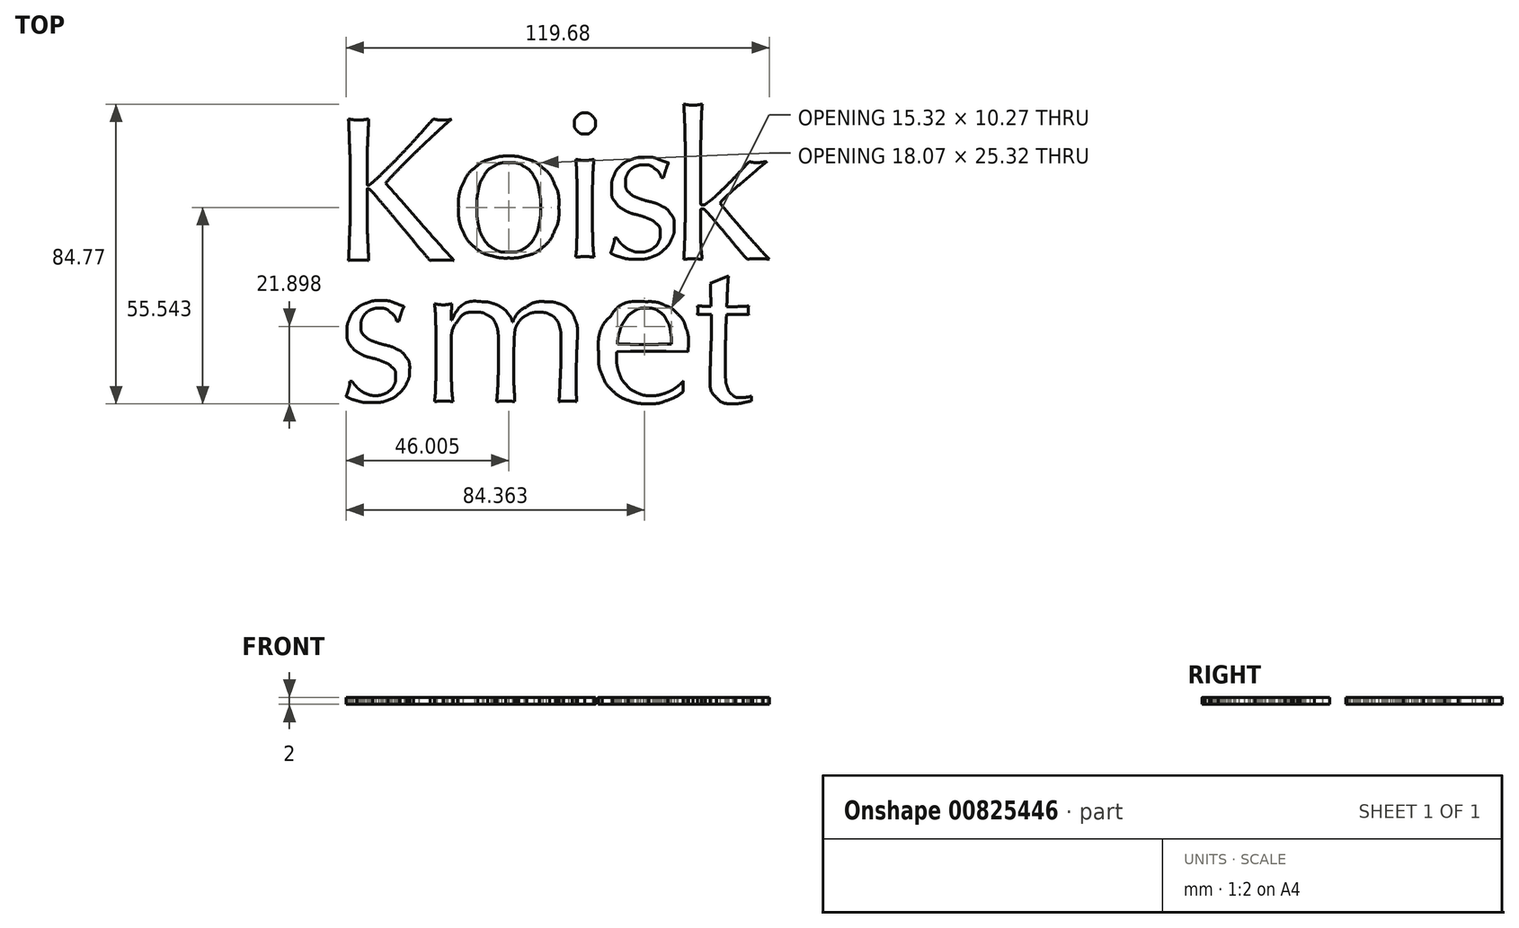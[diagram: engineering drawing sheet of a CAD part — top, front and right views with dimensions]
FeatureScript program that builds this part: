
annotation { "Feature Type Name" : "Feature", "Feature Type Description" : "" }
export const myFeature = defineFeature(function(context is Context, id is Id, definition is map)
    precondition{}
    {
        {
            var Q0;
            Q0=qCreatedBy(makeId("Top.planeOp"),FACE);
            var sketch = newSketch(context, id + "F0", { "sketchPlane" : qUnion([Q0])});
            skFitSpline(sketch, "E0", {"points": [v(-58.08, -1.08) * mm, v(-57.19, -1) * mm, v(-56.23, -0.96) * mm, v(-55.23, -0.96) * mm]});
            skFitSpline(sketch, "E1", {"points": [v(-55.23, -0.96) * mm, v(-54.22, -0.96) * mm, v(-53.27, -1) * mm, v(-52.37, -1.08) * mm]});
            skFitSpline(sketch, "E2", {"points": [v(-52.37, -1.08) * mm, v(-52.49, 1.33) * mm, v(-52.6, 3.78) * mm, v(-52.72, 6.26) * mm]});
            skFitSpline(sketch, "E3", {"points": [v(-52.72, 6.26) * mm, v(-52.8, 8.75) * mm, v(-52.84, 11.27) * mm, v(-52.84, 13.83) * mm]});
            skFitSpline(sketch, "E4", {"points": [v(-52.84, 18.9) * mm, v(-52.84, 19.13) * mm, v(-52.74, 19.25) * mm, v(-52.55, 19.25) * mm]});
            skFitSpline(sketch, "E5", {"points": [v(-52.55, 19.25) * mm, v(-52.4, 19.25) * mm, v(-52.16, 19.09) * mm, v(-51.85, 18.78) * mm]});
            skFitSpline(sketch, "E6", {"points": [v(-51.85, 18.78) * mm, v(-51.23, 18.16) * mm, v(-50.28, 17.07) * mm, v(-49, 15.52) * mm]});
            skFitSpline(sketch, "E7", {"points": [v(-49, 15.52) * mm, v(-47.68, 14) * mm, v(-46.22, 12.28) * mm, v(-44.63, 10.34) * mm]});
            skFitSpline(sketch, "E8", {"points": [v(-44.63, 10.34) * mm, v(-43, 8.43) * mm, v(-41.35, 6.46) * mm, v(-39.68, 4.4) * mm]});
            skFitSpline(sketch, "E9", {"points": [v(-39.68, 4.4) * mm, v(-37.97, 2.34) * mm, v(-36.42, 0.52) * mm, v(-35.02, -1.08) * mm]});
            skFitSpline(sketch, "E10", {"points": [v(-35.02, -1.08) * mm, v(-34.48, -1) * mm, v(-33.95, -0.96) * mm, v(-33.45, -0.96) * mm]});
            skFitSpline(sketch, "E11", {"points": [v(-33.45, -0.96) * mm, v(-32.9, -0.96) * mm, v(-32.36, -0.96) * mm, v(-31.82, -0.96) * mm]});
            skFitSpline(sketch, "E12", {"points": [v(-31.82, -0.96) * mm, v(-31.24, -0.96) * mm, v(-30.65, -0.96) * mm, v(-30.07, -0.96) * mm]});
            skFitSpline(sketch, "E13", {"points": [v(-30.07, -0.96) * mm, v(-29.5, -0.96) * mm, v(-28.9, -1) * mm, v(-28.33, -1.08) * mm]});
            skFitSpline(sketch, "E14", {"points": [v(-28.33, -1.08) * mm, v(-31.63, 2.61) * mm, v(-34.89, 6.28) * mm, v(-38.1, 9.93) * mm]});
            skFitSpline(sketch, "E15", {"points": [v(-38.1, 9.93) * mm, v(-41.3, 13.62) * mm, v(-44.45, 17.23) * mm, v(-47.6, 20.76) * mm]});
            skFitSpline(sketch, "E16", {"points": [v(-47.6, 20.76) * mm, v(-46.55, 21.96) * mm, v(-45.25, 23.36) * mm, v(-43.7, 24.95) * mm]});
            skFitSpline(sketch, "E17", {"points": [v(-43.7, 24.95) * mm, v(-42.1, 26.58) * mm, v(-40.46, 28.23) * mm, v(-38.75, 29.9) * mm]});
            skFitSpline(sketch, "E18", {"points": [v(-38.75, 29.9) * mm, v(-37, 31.57) * mm, v(-35.27, 33.2) * mm, v(-33.57, 34.8) * mm]});
            skFitSpline(sketch, "E19", {"points": [v(-33.57, 34.8) * mm, v(-31.86, 36.38) * mm, v(-30.32, 37.76) * mm, v(-28.97, 38.92) * mm]});
            skFitSpline(sketch, "E20", {"points": [v(-28.97, 38.92) * mm, v(-29.43, 38.85) * mm, v(-29.9, 38.77) * mm, v(-30.36, 38.7) * mm]});
            skFitSpline(sketch, "E21", {"points": [v(-30.36, 38.7) * mm, v(-30.83, 38.65) * mm, v(-31.3, 38.63) * mm, v(-31.76, 38.63) * mm]});
            skFitSpline(sketch, "E22", {"points": [v(-31.76, 38.63) * mm, v(-32.15, 38.63) * mm, v(-32.54, 38.65) * mm, v(-32.93, 38.7) * mm]});
            skFitSpline(sketch, "E23", {"points": [v(-32.93, 38.7) * mm, v(-33.31, 38.77) * mm, v(-33.72, 38.85) * mm, v(-34.15, 38.92) * mm]});
            skFitSpline(sketch, "E24", {"points": [v(-34.15, 38.92) * mm, v(-35.5, 37.37) * mm, v(-36.92, 35.76) * mm, v(-38.4, 34.1) * mm]});
            skFitSpline(sketch, "E25", {"points": [v(-38.4, 34.1) * mm, v(-39.87, 32.46) * mm, v(-41.37, 30.85) * mm, v(-42.88, 29.26) * mm]});
            skFitSpline(sketch, "E26", {"points": [v(-42.88, 29.26) * mm, v(-44.4, 27.67) * mm, v(-45.9, 26.13) * mm, v(-47.42, 24.66) * mm]});
            skFitSpline(sketch, "E27", {"points": [v(-47.42, 24.66) * mm, v(-48.9, 23.18) * mm, v(-50.32, 21.87) * mm, v(-51.67, 20.7) * mm]});
            skFitSpline(sketch, "E28", {"points": [v(-51.67, 20.7) * mm, v(-52.06, 20.35) * mm, v(-52.33, 20.18) * mm, v(-52.49, 20.18) * mm]});
            skFitSpline(sketch, "E29", {"points": [v(-52.49, 20.18) * mm, v(-52.72, 20.18) * mm, v(-52.84, 20.33) * mm, v(-52.84, 20.64) * mm]});
            skLineSegment(sketch, "E30", {"start": v(-52.84, 13.83) * mm, "end": v(-52.84, 18.9) * mm});
            skLineSegment(sketch, "E31", {"start": v(-52.84, 18.9) * mm, "end": v(-52.84, 13.83) * mm});
            skFitSpline(sketch, "E32", {"points": [v(-52.84, 23.84) * mm, v(-52.84, 26.4) * mm, v(-52.8, 28.91) * mm, v(-52.72, 31.36) * mm]});
            skFitSpline(sketch, "E33", {"points": [v(-52.72, 31.36) * mm, v(-52.6, 33.84) * mm, v(-52.49, 36.36) * mm, v(-52.37, 38.92) * mm]});
            skFitSpline(sketch, "E34", {"points": [v(-52.37, 38.92) * mm, v(-52.88, 38.85) * mm, v(-53.36, 38.77) * mm, v(-53.83, 38.7) * mm]});
            skFitSpline(sketch, "E35", {"points": [v(-53.83, 38.7) * mm, v(-54.3, 38.65) * mm, v(-54.76, 38.63) * mm, v(-55.23, 38.63) * mm]});
            skFitSpline(sketch, "E36", {"points": [v(-55.23, 38.63) * mm, v(-55.7, 38.63) * mm, v(-56.16, 38.65) * mm, v(-56.62, 38.7) * mm]});
            skFitSpline(sketch, "E37", {"points": [v(-56.62, 38.7) * mm, v(-57.09, 38.77) * mm, v(-57.57, 38.85) * mm, v(-58.08, 38.92) * mm]});
            skFitSpline(sketch, "E38", {"points": [v(-58.08, 38.92) * mm, v(-57.96, 36.36) * mm, v(-57.86, 33.84) * mm, v(-57.79, 31.36) * mm]});
            skFitSpline(sketch, "E39", {"points": [v(-57.79, 31.36) * mm, v(-57.67, 28.91) * mm, v(-57.61, 26.4) * mm, v(-57.61, 23.84) * mm]});
            skLineSegment(sketch, "E40", {"start": v(-52.84, 20.64) * mm, "end": v(-52.84, 23.84) * mm});
            skLineSegment(sketch, "E41", {"start": v(-52.84, 23.84) * mm, "end": v(-52.84, 20.64) * mm});
            skFitSpline(sketch, "E42", {"points": [v(-57.61, 13.83) * mm, v(-57.61, 11.27) * mm, v(-57.67, 8.75) * mm, v(-57.79, 6.26) * mm]});
            skFitSpline(sketch, "E43", {"points": [v(-57.79, 6.26) * mm, v(-57.86, 3.78) * mm, v(-57.96, 1.33) * mm, v(-58.08, -1.08) * mm]});
            skLineSegment(sketch, "E44", {"start": v(-57.61, 23.84) * mm, "end": v(-57.61, 13.83) * mm});
            skLineSegment(sketch, "E45", {"start": v(-57.61, 13.83) * mm, "end": v(-57.61, 23.84) * mm});
            skFitSpline(sketch, "E46", {"points": [v(-21.81, 13.91) * mm, v(-21.81, 15.54) * mm, v(-21.67, 17.12) * mm, v(-21.4, 18.63) * mm]});
            skFitSpline(sketch, "E47", {"points": [v(-21.4, 18.63) * mm, v(-21.1, 20.14) * mm, v(-20.59, 21.48) * mm, v(-19.89, 22.65) * mm]});
            skFitSpline(sketch, "E48", {"points": [v(-19.89, 22.65) * mm, v(-19.2, 23.85) * mm, v(-18.26, 24.8) * mm, v(-17.1, 25.5) * mm]});
            skFitSpline(sketch, "E49", {"points": [v(-17.1, 25.5) * mm, v(-15.93, 26.2) * mm, v(-14.5, 26.55) * mm, v(-12.79, 26.55) * mm]});
            skFitSpline(sketch, "E50", {"points": [v(-12.79, 26.55) * mm, v(-11.08, 26.55) * mm, v(-9.64, 26.2) * mm, v(-8.48, 25.5) * mm]});
            skFitSpline(sketch, "E51", {"points": [v(-8.48, 25.5) * mm, v(-7.31, 24.8) * mm, v(-6.38, 23.85) * mm, v(-5.68, 22.65) * mm]});
            skFitSpline(sketch, "E52", {"points": [v(-5.68, 22.65) * mm, v(-4.98, 21.48) * mm, v(-4.5, 20.14) * mm, v(-4.23, 18.63) * mm]});
            skFitSpline(sketch, "E53", {"points": [v(-4.23, 18.63) * mm, v(-3.92, 17.12) * mm, v(-3.76, 15.54) * mm, v(-3.76, 13.91) * mm]});
            skFitSpline(sketch, "E54", {"points": [v(-3.76, 13.91) * mm, v(-3.76, 12.28) * mm, v(-3.92, 10.71) * mm, v(-4.23, 9.2) * mm]});
            skFitSpline(sketch, "E55", {"points": [v(-4.23, 9.2) * mm, v(-4.5, 7.68) * mm, v(-4.98, 6.32) * mm, v(-5.68, 5.12) * mm]});
            skFitSpline(sketch, "E56", {"points": [v(-5.68, 5.12) * mm, v(-6.38, 3.96) * mm, v(-7.31, 3.03) * mm, v(-8.48, 2.33) * mm]});
            skFitSpline(sketch, "E57", {"points": [v(-8.48, 2.33) * mm, v(-9.64, 1.63) * mm, v(-11.08, 1.28) * mm, v(-12.79, 1.28) * mm]});
            skFitSpline(sketch, "E58", {"points": [v(-12.79, 1.28) * mm, v(-14.5, 1.28) * mm, v(-15.93, 1.63) * mm, v(-17.1, 2.33) * mm]});
            skFitSpline(sketch, "E59", {"points": [v(-17.1, 2.33) * mm, v(-18.26, 3.03) * mm, v(-19.2, 3.96) * mm, v(-19.89, 5.12) * mm]});
            skFitSpline(sketch, "E60", {"points": [v(-19.89, 5.12) * mm, v(-20.59, 6.32) * mm, v(-21.1, 7.68) * mm, v(-21.4, 9.2) * mm]});
            skFitSpline(sketch, "E61", {"points": [v(-21.4, 9.2) * mm, v(-21.67, 10.71) * mm, v(-21.81, 12.28) * mm, v(-21.81, 13.91) * mm]});
            skFitSpline(sketch, "E62", {"points": [v(-26.93, 13.91) * mm, v(-26.93, 11.27) * mm, v(-26.53, 9.02) * mm, v(-25.71, 7.16) * mm]});
            skFitSpline(sketch, "E63", {"points": [v(-25.71, 7.16) * mm, v(-24.86, 5.33) * mm, v(-23.75, 3.84) * mm, v(-22.4, 2.68) * mm]});
            skFitSpline(sketch, "E64", {"points": [v(-22.4, 2.68) * mm, v(-21.03, 1.55) * mm, v(-19.52, 0.75) * mm, v(-17.85, 0.29) * mm]});
            skFitSpline(sketch, "E65", {"points": [v(-17.85, 0.29) * mm, v(-16.14, -0.18) * mm, v(-14.45, -0.4) * mm, v(-12.79, -0.4) * mm]});
            skFitSpline(sketch, "E66", {"points": [v(-12.79, -0.4) * mm, v(-11.08, -0.4) * mm, v(-9.39, -0.18) * mm, v(-7.72, 0.29) * mm]});
            skFitSpline(sketch, "E67", {"points": [v(-7.72, 0.29) * mm, v(-6.05, 0.75) * mm, v(-4.54, 1.55) * mm, v(-3.18, 2.68) * mm]});
            skFitSpline(sketch, "E68", {"points": [v(-3.18, 2.68) * mm, v(-1.82, 3.84) * mm, v(-0.73, 5.33) * mm, v(0.08, 7.16) * mm]});
            skFitSpline(sketch, "E69", {"points": [v(0.08, 7.16) * mm, v(0.94, 9.02) * mm, v(1.36, 11.27) * mm, v(1.36, 13.91) * mm]});
            skFitSpline(sketch, "E70", {"points": [v(1.36, 13.91) * mm, v(1.36, 16.55) * mm, v(0.94, 18.78) * mm, v(0.08, 20.6) * mm]});
            skFitSpline(sketch, "E71", {"points": [v(0.08, 20.6) * mm, v(-0.73, 22.47) * mm, v(-1.82, 23.97) * mm, v(-3.18, 25.1) * mm]});
            skFitSpline(sketch, "E72", {"points": [v(-3.18, 25.1) * mm, v(-4.54, 26.26) * mm, v(-6.05, 27.1) * mm, v(-7.72, 27.6) * mm]});
            skFitSpline(sketch, "E73", {"points": [v(-7.72, 27.6) * mm, v(-9.39, 28.14) * mm, v(-11.08, 28.41) * mm, v(-12.79, 28.41) * mm]});
            skFitSpline(sketch, "E74", {"points": [v(-12.79, 28.41) * mm, v(-14.45, 28.41) * mm, v(-16.14, 28.14) * mm, v(-17.85, 27.6) * mm]});
            skFitSpline(sketch, "E75", {"points": [v(-17.85, 27.6) * mm, v(-19.52, 27.1) * mm, v(-21.03, 26.26) * mm, v(-22.4, 25.1) * mm]});
            skFitSpline(sketch, "E76", {"points": [v(-22.4, 25.1) * mm, v(-23.75, 23.97) * mm, v(-24.86, 22.47) * mm, v(-25.71, 20.6) * mm]});
            skFitSpline(sketch, "E77", {"points": [v(-25.71, 20.6) * mm, v(-26.53, 18.78) * mm, v(-26.93, 16.55) * mm, v(-26.93, 13.91) * mm]});
            skFitSpline(sketch, "E78", {"points": [v(-57.69, -35.27) * mm, v(-57.69, -35.85) * mm, v(-57.82, -36.59) * mm, v(-58.1, -37.48) * mm]});
            skFitSpline(sketch, "E79", {"points": [v(-58.1, -37.48) * mm, v(-58.33, -38.34) * mm, v(-58.56, -39.02) * mm, v(-58.8, -39.52) * mm]});
            skFitSpline(sketch, "E80", {"points": [v(-58.8, -39.52) * mm, v(-57.98, -39.99) * mm, v(-56.97, -40.4) * mm, v(-55.76, -40.74) * mm]});
            skFitSpline(sketch, "E81", {"points": [v(-55.76, -40.74) * mm, v(-54.56, -41.1) * mm, v(-53.07, -41.27) * mm, v(-51.28, -41.27) * mm]});
            skFitSpline(sketch, "E82", {"points": [v(-51.28, -41.27) * mm, v(-49.65, -41.27) * mm, v(-48.2, -41.03) * mm, v(-46.91, -40.57) * mm]});
            skFitSpline(sketch, "E83", {"points": [v(-46.91, -40.57) * mm, v(-45.63, -40.06) * mm, v(-44.55, -39.38) * mm, v(-43.65, -38.53) * mm]});
            skFitSpline(sketch, "E84", {"points": [v(-43.65, -38.53) * mm, v(-42.72, -37.64) * mm, v(-42.02, -36.65) * mm, v(-41.56, -35.56) * mm]});
            skFitSpline(sketch, "E85", {"points": [v(-41.56, -35.56) * mm, v(-41.05, -34.47) * mm, v(-40.8, -33.37) * mm, v(-40.8, -32.24) * mm]});
            skFitSpline(sketch, "E86", {"points": [v(-40.8, -32.24) * mm, v(-40.8, -30.61) * mm, v(-41.15, -29.33) * mm, v(-41.85, -28.4) * mm]});
            skFitSpline(sketch, "E87", {"points": [v(-41.85, -28.4) * mm, v(-42.5, -27.47) * mm, v(-43.34, -26.75) * mm, v(-44.35, -26.24) * mm]});
            skFitSpline(sketch, "E88", {"points": [v(-44.35, -26.24) * mm, v(-45.36, -25.7) * mm, v(-46.47, -25.3) * mm, v(-47.67, -25.02) * mm]});
            skFitSpline(sketch, "E89", {"points": [v(-47.67, -25.02) * mm, v(-48.87, -24.71) * mm, v(-49.98, -24.36) * mm, v(-51, -23.97) * mm]});
            skFitSpline(sketch, "E90", {"points": [v(-51, -23.97) * mm, v(-52, -23.59) * mm, v(-52.85, -23.06) * mm, v(-53.55, -22.4) * mm]});
            skFitSpline(sketch, "E91", {"points": [v(-53.55, -22.4) * mm, v(-54.21, -21.7) * mm, v(-54.54, -20.73) * mm, v(-54.54, -19.5) * mm]});
            skFitSpline(sketch, "E92", {"points": [v(-54.54, -19.5) * mm, v(-54.54, -18.64) * mm, v(-54.39, -17.9) * mm, v(-54.08, -17.28) * mm]});
            skFitSpline(sketch, "E93", {"points": [v(-54.08, -17.28) * mm, v(-53.77, -16.66) * mm, v(-53.38, -16.15) * mm, v(-52.91, -15.76) * mm]});
            skFitSpline(sketch, "E94", {"points": [v(-52.91, -15.76) * mm, v(-52.45, -15.38) * mm, v(-51.92, -15.08) * mm, v(-51.34, -14.9) * mm]});
            skFitSpline(sketch, "E95", {"points": [v(-51.34, -14.9) * mm, v(-50.76, -14.7) * mm, v(-50.18, -14.6) * mm, v(-49.6, -14.6) * mm]});
            skFitSpline(sketch, "E96", {"points": [v(-49.6, -14.6) * mm, v(-48.27, -14.6) * mm, v(-47.17, -14.97) * mm, v(-46.27, -15.7) * mm]});
            skFitSpline(sketch, "E97", {"points": [v(-46.27, -15.7) * mm, v(-45.38, -16.44) * mm, v(-44.78, -17.28) * mm, v(-44.47, -18.2) * mm]});
            skLineSegment(sketch, "E98", {"start": v(-56.99, -35.27) * mm, "end": v(-57.69, -35.27) * mm});
            skLineSegment(sketch, "E99", {"start": v(-57.69, -35.27) * mm, "end": v(-56.99, -35.27) * mm});
            skFitSpline(sketch, "E100", {"points": [v(-43.77, -18.2) * mm, v(-43.7, -17.74) * mm, v(-43.52, -17.08) * mm, v(-43.25, -16.23) * mm]});
            skFitSpline(sketch, "E101", {"points": [v(-43.25, -16.23) * mm, v(-42.97, -15.38) * mm, v(-42.68, -14.66) * mm, v(-42.37, -14.08) * mm]});
            skFitSpline(sketch, "E102", {"points": [v(-42.37, -14.08) * mm, v(-43.27, -13.77) * mm, v(-44.22, -13.42) * mm, v(-45.23, -13.03) * mm]});
            skFitSpline(sketch, "E103", {"points": [v(-45.23, -13.03) * mm, v(-46.2, -12.64) * mm, v(-47.4, -12.45) * mm, v(-48.84, -12.45) * mm]});
            skFitSpline(sketch, "E104", {"points": [v(-48.84, -12.45) * mm, v(-50.39, -12.45) * mm, v(-51.77, -12.68) * mm, v(-52.97, -13.14) * mm]});
            skFitSpline(sketch, "E105", {"points": [v(-52.97, -13.14) * mm, v(-54.17, -13.57) * mm, v(-55.18, -14.17) * mm, v(-56, -14.95) * mm]});
            skFitSpline(sketch, "E106", {"points": [v(-56, -14.95) * mm, v(-56.81, -15.73) * mm, v(-57.43, -16.66) * mm, v(-57.86, -17.74) * mm]});
            skFitSpline(sketch, "E107", {"points": [v(-57.86, -17.74) * mm, v(-58.29, -18.8) * mm, v(-58.5, -19.96) * mm, v(-58.5, -21.24) * mm]});
            skFitSpline(sketch, "E108", {"points": [v(-58.5, -21.24) * mm, v(-58.5, -22.87) * mm, v(-58.17, -24.15) * mm, v(-57.51, -25.08) * mm]});
            skFitSpline(sketch, "E109", {"points": [v(-57.51, -25.08) * mm, v(-56.81, -26.01) * mm, v(-55.96, -26.77) * mm, v(-54.95, -27.35) * mm]});
            skFitSpline(sketch, "E110", {"points": [v(-54.95, -27.35) * mm, v(-53.94, -27.9) * mm, v(-52.83, -28.32) * mm, v(-51.63, -28.63) * mm]});
            skFitSpline(sketch, "E111", {"points": [v(-51.63, -28.63) * mm, v(-50.43, -28.94) * mm, v(-49.32, -29.31) * mm, v(-48.31, -29.74) * mm]});
            skFitSpline(sketch, "E112", {"points": [v(-48.31, -29.74) * mm, v(-47.3, -30.13) * mm, v(-46.47, -30.65) * mm, v(-45.8, -31.31) * mm]});
            skFitSpline(sketch, "E113", {"points": [v(-45.8, -31.31) * mm, v(-45.1, -31.93) * mm, v(-44.76, -32.84) * mm, v(-44.76, -34.05) * mm]});
            skFitSpline(sketch, "E114", {"points": [v(-44.76, -34.05) * mm, v(-44.76, -34.9) * mm, v(-44.92, -35.66) * mm, v(-45.23, -36.32) * mm]});
            skFitSpline(sketch, "E115", {"points": [v(-45.23, -36.32) * mm, v(-45.54, -36.98) * mm, v(-45.96, -37.52) * mm, v(-46.5, -37.95) * mm]});
            skFitSpline(sketch, "E116", {"points": [v(-46.5, -37.95) * mm, v(-47.01, -38.37) * mm, v(-47.61, -38.7) * mm, v(-48.31, -38.94) * mm]});
            skFitSpline(sketch, "E117", {"points": [v(-48.31, -38.94) * mm, v(-48.97, -39.17) * mm, v(-49.67, -39.29) * mm, v(-50.4, -39.29) * mm]});
            skFitSpline(sketch, "E118", {"points": [v(-50.4, -39.29) * mm, v(-51.22, -39.29) * mm, v(-52, -39.15) * mm, v(-52.74, -38.88) * mm]});
            skFitSpline(sketch, "E119", {"points": [v(-52.74, -38.88) * mm, v(-53.44, -38.6) * mm, v(-54.08, -38.28) * mm, v(-54.66, -37.89) * mm]});
            skFitSpline(sketch, "E120", {"points": [v(-54.66, -37.89) * mm, v(-55.2, -37.46) * mm, v(-55.69, -37.02) * mm, v(-56.11, -36.55) * mm]});
            skFitSpline(sketch, "E121", {"points": [v(-56.11, -36.55) * mm, v(-56.5, -36.08) * mm, v(-56.8, -35.66) * mm, v(-56.99, -35.27) * mm]});
            skLineSegment(sketch, "E122", {"start": v(-44.47, -18.2) * mm, "end": v(-43.77, -18.2) * mm});
            skLineSegment(sketch, "E123", {"start": v(-43.77, -18.2) * mm, "end": v(-44.47, -18.2) * mm});
            skFitSpline(sketch, "E124", {"points": [v(-33.33, -30.28) * mm, v(-33.33, -32.03) * mm, v(-33.36, -33.87) * mm, v(-33.44, -35.81) * mm]});
            skFitSpline(sketch, "E125", {"points": [v(-33.44, -35.81) * mm, v(-33.48, -37.72) * mm, v(-33.6, -39.44) * mm, v(-33.8, -41) * mm]});
            skFitSpline(sketch, "E126", {"points": [v(-33.8, -41) * mm, v(-32.9, -40.92) * mm, v(-32.03, -40.88) * mm, v(-31.17, -40.88) * mm]});
            skFitSpline(sketch, "E127", {"points": [v(-31.17, -40.88) * mm, v(-30.32, -40.88) * mm, v(-29.44, -40.92) * mm, v(-28.55, -41) * mm]});
            skFitSpline(sketch, "E128", {"points": [v(-28.55, -41) * mm, v(-28.75, -39.44) * mm, v(-28.88, -37.72) * mm, v(-28.96, -35.81) * mm]});
            skFitSpline(sketch, "E129", {"points": [v(-28.96, -35.81) * mm, v(-29, -33.87) * mm, v(-29.02, -32.03) * mm, v(-29.02, -30.28) * mm]});
            skLineSegment(sketch, "E130", {"start": v(-33.33, -24.23) * mm, "end": v(-33.33, -30.28) * mm});
            skLineSegment(sketch, "E131", {"start": v(-33.33, -30.28) * mm, "end": v(-33.33, -24.23) * mm});
            skFitSpline(sketch, "E132", {"points": [v(-29.02, -25.33) * mm, v(-29.02, -22.3) * mm, v(-28.42, -19.96) * mm, v(-27.21, -18.29) * mm]});
            skFitSpline(sketch, "E133", {"points": [v(-27.21, -18.29) * mm, v(-26, -16.62) * mm, v(-24.13, -15.78) * mm, v(-21.56, -15.78) * mm]});
            skFitSpline(sketch, "E134", {"points": [v(-21.56, -15.78) * mm, v(-20.6, -15.78) * mm, v(-19.66, -16.06) * mm, v(-18.77, -16.6) * mm]});
            skFitSpline(sketch, "E135", {"points": [v(-18.77, -16.6) * mm, v(-17.84, -17.1) * mm, v(-17.16, -17.73) * mm, v(-16.73, -18.46) * mm]});
            skFitSpline(sketch, "E136", {"points": [v(-16.73, -18.46) * mm, v(-16.5, -18.93) * mm, v(-16.32, -19.36) * mm, v(-16.2, -19.74) * mm]});
            skFitSpline(sketch, "E137", {"points": [v(-16.2, -19.74) * mm, v(-16.05, -20.13) * mm, v(-15.94, -20.64) * mm, v(-15.86, -21.26) * mm]});
            skFitSpline(sketch, "E138", {"points": [v(-15.86, -21.26) * mm, v(-15.78, -21.84) * mm, v(-15.74, -22.66) * mm, v(-15.74, -23.7) * mm]});
            skFitSpline(sketch, "E139", {"points": [v(-15.74, -23.7) * mm, v(-15.7, -24.71) * mm, v(-15.68, -26.13) * mm, v(-15.68, -27.95) * mm]});
            skFitSpline(sketch, "E140", {"points": [v(-15.68, -27.95) * mm, v(-15.68, -30.09) * mm, v(-15.72, -32.26) * mm, v(-15.8, -34.47) * mm]});
            skFitSpline(sketch, "E141", {"points": [v(-15.8, -34.47) * mm, v(-15.88, -36.69) * mm, v(-16.01, -38.86) * mm, v(-16.2, -41) * mm]});
            skFitSpline(sketch, "E142", {"points": [v(-16.2, -41) * mm, v(-15.32, -40.92) * mm, v(-14.46, -40.88) * mm, v(-13.65, -40.88) * mm]});
            skFitSpline(sketch, "E143", {"points": [v(-13.65, -40.88) * mm, v(-12.83, -40.88) * mm, v(-11.98, -40.92) * mm, v(-11.08, -41) * mm]});
            skFitSpline(sketch, "E144", {"points": [v(-11.08, -41) * mm, v(-11.16, -39.37) * mm, v(-11.24, -37.87) * mm, v(-11.32, -36.51) * mm]});
            skFitSpline(sketch, "E145", {"points": [v(-11.32, -36.51) * mm, v(-11.36, -35.12) * mm, v(-11.38, -33.58) * mm, v(-11.38, -31.91) * mm]});
            skFitSpline(sketch, "E146", {"points": [v(-11.38, -31.91) * mm, v(-11.38, -29.16) * mm, v(-11.36, -27) * mm, v(-11.32, -25.45) * mm]});
            skFitSpline(sketch, "E147", {"points": [v(-11.32, -25.45) * mm, v(-11.28, -23.86) * mm, v(-11.22, -22.64) * mm, v(-11.14, -21.78) * mm]});
            skFitSpline(sketch, "E148", {"points": [v(-11.14, -21.78) * mm, v(-11.03, -20.89) * mm, v(-10.9, -20.23) * mm, v(-10.74, -19.8) * mm]});
            skFitSpline(sketch, "E149", {"points": [v(-10.74, -19.8) * mm, v(-10.54, -19.38) * mm, v(-10.29, -18.95) * mm, v(-9.98, -18.52) * mm]});
            skFitSpline(sketch, "E150", {"points": [v(-9.98, -18.52) * mm, v(-9.43, -17.78) * mm, v(-8.68, -17.14) * mm, v(-7.7, -16.6) * mm]});
            skFitSpline(sketch, "E151", {"points": [v(-7.7, -16.6) * mm, v(-6.74, -16.06) * mm, v(-5.55, -15.78) * mm, v(-4.16, -15.78) * mm]});
            skFitSpline(sketch, "E152", {"points": [v(-4.16, -15.78) * mm, v(-3, -15.78) * mm, v(-2.02, -15.98) * mm, v(-1.24, -16.37) * mm]});
            skFitSpline(sketch, "E153", {"points": [v(-1.24, -16.37) * mm, v(-0.47, -16.72) * mm, v(0.15, -17.2) * mm, v(0.62, -17.82) * mm]});
            skFitSpline(sketch, "E154", {"points": [v(0.62, -17.82) * mm, v(1.08, -18.44) * mm, v(1.41, -19.18) * mm, v(1.6, -20.04) * mm]});
            skFitSpline(sketch, "E155", {"points": [v(1.6, -20.04) * mm, v(1.84, -20.89) * mm, v(1.96, -21.8) * mm, v(1.96, -22.77) * mm]});
            skFitSpline(sketch, "E156", {"points": [v(1.96, -22.77) * mm, v(1.96, -28.05) * mm, v(1.88, -32.17) * mm, v(1.72, -35.12) * mm]});
            skFitSpline(sketch, "E157", {"points": [v(1.72, -35.12) * mm, v(1.6, -38.07) * mm, v(1.5, -40.03) * mm, v(1.38, -41) * mm]});
            skFitSpline(sketch, "E158", {"points": [v(1.38, -41) * mm, v(1.8, -40.92) * mm, v(2.23, -40.88) * mm, v(2.66, -40.88) * mm]});
            skFitSpline(sketch, "E159", {"points": [v(2.66, -40.88) * mm, v(3.08, -40.88) * mm, v(3.51, -40.88) * mm, v(3.94, -40.88) * mm]});
            skFitSpline(sketch, "E160", {"points": [v(3.94, -40.88) * mm, v(4.33, -40.88) * mm, v(4.73, -40.88) * mm, v(5.16, -40.88) * mm]});
            skFitSpline(sketch, "E161", {"points": [v(5.16, -40.88) * mm, v(5.59, -40.88) * mm, v(6.01, -40.92) * mm, v(6.44, -41) * mm]});
            skFitSpline(sketch, "E162", {"points": [v(6.44, -41) * mm, v(6.36, -39.87) * mm, v(6.3, -38.82) * mm, v(6.27, -37.85) * mm]});
            skFitSpline(sketch, "E163", {"points": [v(6.27, -37.85) * mm, v(6.27, -36.88) * mm, v(6.27, -35.87) * mm, v(6.27, -34.82) * mm]});
            skFitSpline(sketch, "E164", {"points": [v(6.27, -34.82) * mm, v(6.27, -33.12) * mm, v(6.29, -31.62) * mm, v(6.32, -30.34) * mm]});
            skFitSpline(sketch, "E165", {"points": [v(6.32, -30.34) * mm, v(6.36, -29.02) * mm, v(6.4, -27.86) * mm, v(6.44, -26.85) * mm]});
            skFitSpline(sketch, "E166", {"points": [v(6.44, -26.85) * mm, v(6.48, -25.8) * mm, v(6.52, -24.89) * mm, v(6.56, -24.11) * mm]});
            skFitSpline(sketch, "E167", {"points": [v(6.56, -24.11) * mm, v(6.6, -23.33) * mm, v(6.62, -22.62) * mm, v(6.62, -21.96) * mm]});
            skFitSpline(sketch, "E168", {"points": [v(6.62, -21.96) * mm, v(6.62, -20.33) * mm, v(6.38, -18.93) * mm, v(5.92, -17.76) * mm]});
            skFitSpline(sketch, "E169", {"points": [v(5.92, -17.76) * mm, v(5.5, -16.6) * mm, v(4.87, -15.65) * mm, v(4.05, -14.91) * mm]});
            skFitSpline(sketch, "E170", {"points": [v(4.05, -14.91) * mm, v(3.28, -14.17) * mm, v(2.35, -13.63) * mm, v(1.26, -13.28) * mm]});
            skFitSpline(sketch, "E171", {"points": [v(1.26, -13.28) * mm, v(0.17, -12.93) * mm, v(-1.01, -12.76) * mm, v(-2.3, -12.76) * mm]});
            skFitSpline(sketch, "E172", {"points": [v(-2.3, -12.76) * mm, v(-4.39, -12.76) * mm, v(-6.25, -13.26) * mm, v(-7.88, -14.27) * mm]});
            skFitSpline(sketch, "E173", {"points": [v(-7.88, -14.27) * mm, v(-9.47, -15.24) * mm, v(-10.74, -16.66) * mm, v(-11.67, -18.52) * mm]});
            skLineSegment(sketch, "E174", {"start": v(-29.02, -30.28) * mm, "end": v(-29.02, -25.33) * mm});
            skLineSegment(sketch, "E175", {"start": v(-29.02, -25.33) * mm, "end": v(-29.02, -30.28) * mm});
            skFitSpline(sketch, "E176", {"points": [v(-11.78, -18.52) * mm, v(-11.98, -17.7) * mm, v(-12.35, -16.95) * mm, v(-12.89, -16.25) * mm]});
            skFitSpline(sketch, "E177", {"points": [v(-12.89, -16.25) * mm, v(-13.43, -15.51) * mm, v(-14.1, -14.9) * mm, v(-14.87, -14.39) * mm]});
            skFitSpline(sketch, "E178", {"points": [v(-14.87, -14.39) * mm, v(-15.6, -13.88) * mm, v(-16.44, -13.5) * mm, v(-17.37, -13.22) * mm]});
            skFitSpline(sketch, "E179", {"points": [v(-17.37, -13.22) * mm, v(-18.3, -12.91) * mm, v(-19.26, -12.76) * mm, v(-20.23, -12.76) * mm]});
            skFitSpline(sketch, "E180", {"points": [v(-20.23, -12.76) * mm, v(-23.95, -12.76) * mm, v(-26.84, -14.5) * mm, v(-28.9, -18) * mm]});
            skLineSegment(sketch, "E181", {"start": v(-11.67, -18.52) * mm, "end": v(-11.78, -18.52) * mm});
            skLineSegment(sketch, "E182", {"start": v(-11.78, -18.52) * mm, "end": v(-11.67, -18.52) * mm});
            skFitSpline(sketch, "E183", {"points": [v(-29.02, -18) * mm, v(-29.02, -16.44) * mm, v(-28.96, -14.9) * mm, v(-28.84, -13.34) * mm]});
            skFitSpline(sketch, "E184", {"points": [v(-28.84, -13.34) * mm, v(-29.35, -13.42) * mm, v(-29.8, -13.5) * mm, v(-30.18, -13.57) * mm]});
            skFitSpline(sketch, "E185", {"points": [v(-30.18, -13.57) * mm, v(-30.53, -13.61) * mm, v(-30.86, -13.63) * mm, v(-31.17, -13.63) * mm]});
            skFitSpline(sketch, "E186", {"points": [v(-31.17, -13.63) * mm, v(-31.83, -13.63) * mm, v(-32.7, -13.53) * mm, v(-33.8, -13.34) * mm]});
            skFitSpline(sketch, "E187", {"points": [v(-33.8, -13.34) * mm, v(-33.6, -15) * mm, v(-33.48, -16.81) * mm, v(-33.44, -18.75) * mm]});
            skFitSpline(sketch, "E188", {"points": [v(-33.44, -18.75) * mm, v(-33.36, -20.66) * mm, v(-33.33, -22.48) * mm, v(-33.33, -24.23) * mm]});
            skLineSegment(sketch, "E189", {"start": v(-28.9, -18) * mm, "end": v(-29.02, -18) * mm});
            skLineSegment(sketch, "E190", {"start": v(-29.02, -18) * mm, "end": v(-28.9, -18) * mm});
            skFitSpline(sketch, "E191", {"points": [v(26.06, -14.62) * mm, v(27.58, -14.62) * mm, v(28.8, -14.95) * mm, v(29.73, -15.61) * mm]});
            skFitSpline(sketch, "E192", {"points": [v(29.73, -15.61) * mm, v(30.66, -16.27) * mm, v(31.38, -17.1) * mm, v(31.89, -18.11) * mm]});
            skFitSpline(sketch, "E193", {"points": [v(31.89, -18.11) * mm, v(32.43, -19.12) * mm, v(32.78, -20.2) * mm, v(32.93, -21.37) * mm]});
            skFitSpline(sketch, "E194", {"points": [v(32.93, -21.37) * mm, v(33.13, -22.54) * mm, v(33.23, -23.65) * mm, v(33.23, -24.7) * mm]});
            skFitSpline(sketch, "E195", {"points": [v(33.23, -24.7) * mm, v(31.98, -24.73) * mm, v(30.7, -24.77) * mm, v(29.38, -24.8) * mm]});
            skFitSpline(sketch, "E196", {"points": [v(29.38, -24.8) * mm, v(28.06, -24.85) * mm, v(26.76, -24.87) * mm, v(25.48, -24.87) * mm]});
            skFitSpline(sketch, "E197", {"points": [v(25.48, -24.87) * mm, v(24.24, -24.87) * mm, v(22.96, -24.85) * mm, v(21.64, -24.8) * mm]});
            skFitSpline(sketch, "E198", {"points": [v(21.64, -24.8) * mm, v(20.36, -24.77) * mm, v(19.12, -24.73) * mm, v(17.91, -24.7) * mm]});
            skFitSpline(sketch, "E199", {"points": [v(17.91, -24.7) * mm, v(18, -23.65) * mm, v(18.18, -22.54) * mm, v(18.5, -21.37) * mm]});
            skFitSpline(sketch, "E200", {"points": [v(18.5, -21.37) * mm, v(18.84, -20.17) * mm, v(19.33, -19.08) * mm, v(19.95, -18.11) * mm]});
            skFitSpline(sketch, "E201", {"points": [v(19.95, -18.11) * mm, v(20.61, -17.1) * mm, v(21.43, -16.27) * mm, v(22.4, -15.61) * mm]});
            skFitSpline(sketch, "E202", {"points": [v(22.4, -15.61) * mm, v(23.4, -14.95) * mm, v(24.63, -14.62) * mm, v(26.06, -14.62) * mm]});
            skFitSpline(sketch, "E203", {"points": [v(12.61, -28.07) * mm, v(12.61, -30.01) * mm, v(12.94, -31.82) * mm, v(13.6, -33.49) * mm]});
            skFitSpline(sketch, "E204", {"points": [v(13.6, -33.49) * mm, v(14.3, -35.15) * mm, v(15.27, -36.6) * mm, v(16.52, -37.85) * mm]});
            skFitSpline(sketch, "E205", {"points": [v(16.52, -37.85) * mm, v(17.8, -39.06) * mm, v(19.3, -39.99) * mm, v(21, -40.65) * mm]});
            skFitSpline(sketch, "E206", {"points": [v(21, -40.65) * mm, v(22.75, -41.27) * mm, v(24.67, -41.58) * mm, v(26.76, -41.58) * mm]});
            skFitSpline(sketch, "E207", {"points": [v(26.76, -41.58) * mm, v(28.63, -41.58) * mm, v(30.41, -41.25) * mm, v(32.12, -40.59) * mm]});
            skFitSpline(sketch, "E208", {"points": [v(32.12, -40.59) * mm, v(33.87, -39.93) * mm, v(35.32, -39.13) * mm, v(36.49, -38.2) * mm]});
            skFitSpline(sketch, "E209", {"points": [v(36.54, -35.17) * mm, v(36.04, -35.76) * mm, v(35.44, -36.3) * mm, v(34.74, -36.8) * mm]});
            skFitSpline(sketch, "E210", {"points": [v(34.74, -36.8) * mm, v(34.08, -37.3) * mm, v(33.36, -37.75) * mm, v(32.59, -38.14) * mm]});
            skFitSpline(sketch, "E211", {"points": [v(32.59, -38.14) * mm, v(31.8, -38.5) * mm, v(31.01, -38.78) * mm, v(30.2, -39.02) * mm]});
            skFitSpline(sketch, "E212", {"points": [v(30.2, -39.02) * mm, v(29.38, -39.21) * mm, v(28.59, -39.3) * mm, v(27.81, -39.3) * mm]});
            skFitSpline(sketch, "E213", {"points": [v(27.81, -39.3) * mm, v(26.18, -39.3) * mm, v(24.74, -39.04) * mm, v(23.5, -38.5) * mm]});
            skFitSpline(sketch, "E214", {"points": [v(23.5, -38.5) * mm, v(22.26, -37.91) * mm, v(21.21, -37.15) * mm, v(20.36, -36.22) * mm]});
            skFitSpline(sketch, "E215", {"points": [v(20.36, -36.22) * mm, v(19.5, -35.25) * mm, v(18.84, -34.1) * mm, v(18.38, -32.79) * mm]});
            skFitSpline(sketch, "E216", {"points": [v(18.38, -32.79) * mm, v(17.95, -31.47) * mm, v(17.74, -30.05) * mm, v(17.74, -28.54) * mm]});
            skLineSegment(sketch, "E217", {"start": v(36.49, -38.2) * mm, "end": v(36.84, -35.35) * mm});
            skLineSegment(sketch, "E218", {"start": v(36.84, -35.35) * mm, "end": v(36.54, -35.17) * mm});
            skLineSegment(sketch, "E219", {"start": v(36.54, -35.17) * mm, "end": v(36.49, -38.2) * mm});
            skFitSpline(sketch, "E220", {"points": [v(17.74, -27.78) * mm, v(17.74, -27.4) * mm, v(17.76, -27.1) * mm, v(17.8, -26.9) * mm]});
            skFitSpline(sketch, "E221", {"points": [v(17.8, -26.9) * mm, v(19.08, -26.87) * mm, v(20.34, -26.83) * mm, v(21.58, -26.79) * mm]});
            skFitSpline(sketch, "E222", {"points": [v(21.58, -26.79) * mm, v(22.86, -26.75) * mm, v(24.14, -26.73) * mm, v(25.42, -26.73) * mm]});
            skFitSpline(sketch, "E223", {"points": [v(25.42, -26.73) * mm, v(27.52, -26.73) * mm, v(29.6, -26.75) * mm, v(31.65, -26.79) * mm]});
            skFitSpline(sketch, "E224", {"points": [v(31.65, -26.79) * mm, v(33.71, -26.83) * mm, v(35.79, -26.87) * mm, v(37.88, -26.9) * mm]});
            skFitSpline(sketch, "E225", {"points": [v(37.88, -26.9) * mm, v(37.92, -26.52) * mm, v(37.94, -26.15) * mm, v(37.94, -25.8) * mm]});
            skFitSpline(sketch, "E226", {"points": [v(37.94, -25.8) * mm, v(37.98, -25.41) * mm, v(38, -25.02) * mm, v(38, -24.64) * mm]});
            skFitSpline(sketch, "E227", {"points": [v(38, -24.64) * mm, v(38, -23) * mm, v(37.75, -21.47) * mm, v(37.24, -20.04) * mm]});
            skFitSpline(sketch, "E228", {"points": [v(37.24, -20.04) * mm, v(36.78, -18.6) * mm, v(36.04, -17.36) * mm, v(35.03, -16.3) * mm]});
            skFitSpline(sketch, "E229", {"points": [v(35.03, -16.3) * mm, v(34.02, -15.22) * mm, v(32.76, -14.37) * mm, v(31.25, -13.75) * mm]});
            skFitSpline(sketch, "E230", {"points": [v(31.25, -13.75) * mm, v(29.77, -13.09) * mm, v(28, -12.76) * mm, v(25.95, -12.76) * mm]});
            skFitSpline(sketch, "E231", {"points": [v(25.95, -12.76) * mm, v(21.6, -12.76) * mm, v(18.28, -14.12) * mm, v(16, -16.83) * mm]});
            skFitSpline(sketch, "E232", {"points": [v(16, -16.83) * mm, v(13.74, -19.55) * mm, v(12.61, -23.3) * mm, v(12.61, -28.07) * mm]});
            skLineSegment(sketch, "E233", {"start": v(17.74, -28.54) * mm, "end": v(17.74, -27.78) * mm});
            skLineSegment(sketch, "E234", {"start": v(17.74, -27.78) * mm, "end": v(17.74, -28.54) * mm});
            skFitSpline(sketch, "E235", {"points": [v(44.17, -7.58) * mm, v(44.25, -8.82) * mm, v(44.3, -10.02) * mm, v(44.3, -11.19) * mm]});
            skFitSpline(sketch, "E236", {"points": [v(44.3, -11.19) * mm, v(44.33, -12.35) * mm, v(44.37, -13.32) * mm, v(44.4, -14.1) * mm]});
            skFitSpline(sketch, "E237", {"points": [v(44.4, -14.1) * mm, v(43.6, -14.1) * mm, v(42.31, -14.04) * mm, v(40.56, -13.92) * mm]});
            skFitSpline(sketch, "E238", {"points": [v(40.56, -13.92) * mm, v(40.6, -14.12) * mm, v(40.62, -14.3) * mm, v(40.62, -14.5) * mm]});
            skFitSpline(sketch, "E239", {"points": [v(40.62, -14.5) * mm, v(40.66, -14.7) * mm, v(40.68, -14.9) * mm, v(40.68, -15.09) * mm]});
            skFitSpline(sketch, "E240", {"points": [v(40.68, -15.09) * mm, v(40.68, -15.32) * mm, v(40.66, -15.55) * mm, v(40.62, -15.78) * mm]});
            skFitSpline(sketch, "E241", {"points": [v(40.62, -15.78) * mm, v(40.62, -15.98) * mm, v(40.6, -16.2) * mm, v(40.56, -16.43) * mm]});
            skFitSpline(sketch, "E242", {"points": [v(40.56, -16.43) * mm, v(40.95, -16.39) * mm, v(41.32, -16.37) * mm, v(41.67, -16.37) * mm]});
            skFitSpline(sketch, "E243", {"points": [v(41.67, -16.37) * mm, v(42.02, -16.33) * mm, v(42.35, -16.3) * mm, v(42.66, -16.3) * mm]});
            skLineSegment(sketch, "E244", {"start": v(49, -5.54) * mm, "end": v(44.17, -7.58) * mm});
            skLineSegment(sketch, "E245", {"start": v(44.17, -7.58) * mm, "end": v(49, -5.54) * mm});
            skFitSpline(sketch, "E246", {"points": [v(44.52, -16.3) * mm, v(44.52, -18.48) * mm, v(44.5, -20.46) * mm, v(44.47, -22.25) * mm]});
            skFitSpline(sketch, "E247", {"points": [v(44.47, -22.25) * mm, v(44.43, -24) * mm, v(44.37, -25.6) * mm, v(44.3, -27.08) * mm]});
            skFitSpline(sketch, "E248", {"points": [v(44.3, -27.08) * mm, v(44.25, -28.52) * mm, v(44.21, -29.86) * mm, v(44.17, -31.1) * mm]});
            skFitSpline(sketch, "E249", {"points": [v(44.17, -31.1) * mm, v(44.14, -32.3) * mm, v(44.12, -33.43) * mm, v(44.12, -34.47) * mm]});
            skFitSpline(sketch, "E250", {"points": [v(44.12, -34.47) * mm, v(44.12, -36.8) * mm, v(44.7, -38.57) * mm, v(45.86, -39.77) * mm]});
            skFitSpline(sketch, "E251", {"points": [v(45.86, -39.77) * mm, v(47.03, -40.98) * mm, v(48.83, -41.58) * mm, v(51.28, -41.58) * mm]});
            skFitSpline(sketch, "E252", {"points": [v(51.28, -41.58) * mm, v(52.02, -41.58) * mm, v(52.77, -41.48) * mm, v(53.55, -41.29) * mm]});
            skFitSpline(sketch, "E253", {"points": [v(53.55, -41.29) * mm, v(54.36, -41.13) * mm, v(55.1, -41) * mm, v(55.76, -40.88) * mm]});
            skLineSegment(sketch, "E254", {"start": v(42.66, -16.3) * mm, "end": v(44.52, -16.3) * mm});
            skLineSegment(sketch, "E255", {"start": v(44.52, -16.3) * mm, "end": v(42.66, -16.3) * mm});
            skFitSpline(sketch, "E256", {"points": [v(55.76, -39.48) * mm, v(55.37, -39.6) * mm, v(54.9, -39.7) * mm, v(54.36, -39.77) * mm]});
            skFitSpline(sketch, "E257", {"points": [v(54.36, -39.77) * mm, v(53.86, -39.85) * mm, v(53.45, -39.89) * mm, v(53.14, -39.89) * mm]});
            skFitSpline(sketch, "E258", {"points": [v(53.14, -39.89) * mm, v(51.98, -39.89) * mm, v(51.08, -39.64) * mm, v(50.46, -39.13) * mm]});
            skFitSpline(sketch, "E259", {"points": [v(50.46, -39.13) * mm, v(49.84, -38.63) * mm, v(49.38, -37.97) * mm, v(49.07, -37.15) * mm]});
            skFitSpline(sketch, "E260", {"points": [v(49.07, -37.15) * mm, v(48.76, -36.3) * mm, v(48.56, -35.35) * mm, v(48.48, -34.3) * mm]});
            skFitSpline(sketch, "E261", {"points": [v(48.48, -34.3) * mm, v(48.44, -33.25) * mm, v(48.43, -32.18) * mm, v(48.43, -31.1) * mm]});
            skFitSpline(sketch, "E262", {"points": [v(48.43, -31.1) * mm, v(48.43, -29.82) * mm, v(48.43, -28.36) * mm, v(48.43, -26.73) * mm]});
            skFitSpline(sketch, "E263", {"points": [v(48.43, -26.73) * mm, v(48.46, -25.1) * mm, v(48.5, -23.55) * mm, v(48.54, -22.07) * mm]});
            skFitSpline(sketch, "E264", {"points": [v(48.54, -22.07) * mm, v(48.58, -20.56) * mm, v(48.62, -19.26) * mm, v(48.66, -18.17) * mm]});
            skFitSpline(sketch, "E265", {"points": [v(48.66, -18.17) * mm, v(48.74, -17.09) * mm, v(48.8, -16.46) * mm, v(48.83, -16.3) * mm]});
            skLineSegment(sketch, "E266", {"start": v(55.76, -40.88) * mm, "end": v(55.76, -39.48) * mm});
            skLineSegment(sketch, "E267", {"start": v(55.76, -39.48) * mm, "end": v(55.76, -40.88) * mm});
            skFitSpline(sketch, "E268", {"points": [v(51.69, -16.3) * mm, v(52.3, -16.3) * mm, v(52.89, -16.33) * mm, v(53.43, -16.37) * mm]});
            skFitSpline(sketch, "E269", {"points": [v(53.43, -16.37) * mm, v(53.98, -16.37) * mm, v(54.5, -16.39) * mm, v(55, -16.43) * mm]});
            skFitSpline(sketch, "E270", {"points": [v(55, -16.43) * mm, v(54.97, -16.3) * mm, v(54.95, -16.11) * mm, v(54.95, -15.84) * mm]});
            skLineSegment(sketch, "E271", {"start": v(48.83, -16.3) * mm, "end": v(51.69, -16.3) * mm});
            skLineSegment(sketch, "E272", {"start": v(51.69, -16.3) * mm, "end": v(48.83, -16.3) * mm});
            skFitSpline(sketch, "E273", {"points": [v(54.95, -14.62) * mm, v(54.95, -14.3) * mm, v(54.97, -14.1) * mm, v(55, -13.98) * mm]});
            skFitSpline(sketch, "E274", {"points": [v(55, -13.98) * mm, v(53.65, -14.06) * mm, v(52.38, -14.12) * mm, v(51.22, -14.15) * mm]});
            skFitSpline(sketch, "E275", {"points": [v(51.22, -14.15) * mm, v(50.06, -14.15) * mm, v(49.26, -14.15) * mm, v(48.83, -14.15) * mm]});
            skFitSpline(sketch, "E276", {"points": [v(48.83, -14.15) * mm, v(48.91, -12.72) * mm, v(48.97, -11.3) * mm, v(49, -9.9) * mm]});
            skFitSpline(sketch, "E277", {"points": [v(49, -9.9) * mm, v(49.09, -8.47) * mm, v(49.18, -7.01) * mm, v(49.3, -5.54) * mm]});
            skLineSegment(sketch, "E278", {"start": v(54.95, -15.84) * mm, "end": v(54.95, -15.2) * mm});
            skLineSegment(sketch, "E279", {"start": v(54.95, -15.2) * mm, "end": v(54.95, -14.62) * mm});
            skLineSegment(sketch, "E280", {"start": v(54.95, -14.62) * mm, "end": v(54.95, -15.84) * mm});
            skFitSpline(sketch, "E281", {"points": [v(5.76, 37.65) * mm, v(5.76, 36.83) * mm, v(6.05, 36.13) * mm, v(6.63, 35.55) * mm]});
            skFitSpline(sketch, "E282", {"points": [v(6.63, 35.55) * mm, v(7.21, 34.97) * mm, v(7.91, 34.68) * mm, v(8.73, 34.68) * mm]});
            skFitSpline(sketch, "E283", {"points": [v(8.73, 34.68) * mm, v(9.54, 34.68) * mm, v(10.24, 34.97) * mm, v(10.82, 35.55) * mm]});
            skFitSpline(sketch, "E284", {"points": [v(10.82, 35.55) * mm, v(11.4, 36.13) * mm, v(11.7, 36.83) * mm, v(11.7, 37.65) * mm]});
            skFitSpline(sketch, "E285", {"points": [v(11.7, 37.65) * mm, v(11.7, 38.46) * mm, v(11.4, 39.16) * mm, v(10.82, 39.74) * mm]});
            skFitSpline(sketch, "E286", {"points": [v(10.82, 39.74) * mm, v(10.24, 40.33) * mm, v(9.54, 40.62) * mm, v(8.73, 40.62) * mm]});
            skFitSpline(sketch, "E287", {"points": [v(8.73, 40.62) * mm, v(7.91, 40.62) * mm, v(7.21, 40.33) * mm, v(6.63, 39.74) * mm]});
            skFitSpline(sketch, "E288", {"points": [v(6.63, 39.74) * mm, v(6.05, 39.16) * mm, v(5.76, 38.46) * mm, v(5.76, 37.65) * mm]});
            skLineSegment(sketch, "E289", {"start": v(49.3, -5.54) * mm, "end": v(49, -5.54) * mm});
            skLineSegment(sketch, "E290", {"start": v(49, -5.54) * mm, "end": v(49.3, -5.54) * mm});
            skFitSpline(sketch, "E291", {"points": [v(6.57, 10.57) * mm, v(6.57, 8.83) * mm, v(6.53, 6.98) * mm, v(6.46, 5.04) * mm]});
            skFitSpline(sketch, "E292", {"points": [v(6.46, 5.04) * mm, v(6.42, 3.14) * mm, v(6.3, 1.41) * mm, v(6.1, -0.14) * mm]});
            skFitSpline(sketch, "E293", {"points": [v(6.1, -0.14) * mm, v(7, -0.06) * mm, v(7.87, -0.02) * mm, v(8.73, -0.02) * mm]});
            skFitSpline(sketch, "E294", {"points": [v(8.73, -0.02) * mm, v(9.58, -0.02) * mm, v(10.45, -0.06) * mm, v(11.35, -0.14) * mm]});
            skFitSpline(sketch, "E295", {"points": [v(11.35, -0.14) * mm, v(11.15, 1.41) * mm, v(11.02, 3.14) * mm, v(10.94, 5.04) * mm]});
            skFitSpline(sketch, "E296", {"points": [v(10.94, 5.04) * mm, v(10.9, 6.98) * mm, v(10.88, 8.83) * mm, v(10.88, 10.57) * mm]});
            skLineSegment(sketch, "E297", {"start": v(6.57, 16.63) * mm, "end": v(6.57, 10.57) * mm});
            skLineSegment(sketch, "E298", {"start": v(6.57, 10.57) * mm, "end": v(6.57, 16.63) * mm});
            skFitSpline(sketch, "E299", {"points": [v(10.88, 16.63) * mm, v(10.88, 18.38) * mm, v(10.9, 20.2) * mm, v(10.94, 22.1) * mm]});
            skFitSpline(sketch, "E300", {"points": [v(10.94, 22.1) * mm, v(11.02, 24.04) * mm, v(11.15, 25.85) * mm, v(11.35, 27.52) * mm]});
            skFitSpline(sketch, "E301", {"points": [v(11.35, 27.52) * mm, v(10.26, 27.32) * mm, v(9.39, 27.23) * mm, v(8.73, 27.23) * mm]});
            skFitSpline(sketch, "E302", {"points": [v(8.73, 27.23) * mm, v(8.07, 27.23) * mm, v(7.2, 27.32) * mm, v(6.1, 27.52) * mm]});
            skFitSpline(sketch, "E303", {"points": [v(6.1, 27.52) * mm, v(6.3, 25.85) * mm, v(6.42, 24.04) * mm, v(6.46, 22.1) * mm]});
            skFitSpline(sketch, "E304", {"points": [v(6.46, 22.1) * mm, v(6.53, 20.2) * mm, v(6.57, 18.38) * mm, v(6.57, 16.63) * mm]});
            skLineSegment(sketch, "E305", {"start": v(10.88, 10.57) * mm, "end": v(10.88, 16.63) * mm});
            skLineSegment(sketch, "E306", {"start": v(10.88, 16.63) * mm, "end": v(10.88, 10.57) * mm});
            skFitSpline(sketch, "E307", {"points": [v(17.1, 5.28) * mm, v(17.1, 4.7) * mm, v(16.96, 3.96) * mm, v(16.7, 3.06) * mm]});
            skFitSpline(sketch, "E308", {"points": [v(16.7, 3.06) * mm, v(16.46, 2.2) * mm, v(16.23, 1.53) * mm, v(16, 1.02) * mm]});
            skFitSpline(sketch, "E309", {"points": [v(16, 1.02) * mm, v(16.8, 0.56) * mm, v(17.82, 0.15) * mm, v(19.02, -0.2) * mm]});
            skFitSpline(sketch, "E310", {"points": [v(19.02, -0.2) * mm, v(20.22, -0.55) * mm, v(21.72, -0.72) * mm, v(23.5, -0.72) * mm]});
            skFitSpline(sketch, "E311", {"points": [v(23.5, -0.72) * mm, v(25.13, -0.72) * mm, v(26.59, -0.49) * mm, v(27.87, -0.02) * mm]});
            skFitSpline(sketch, "E312", {"points": [v(27.87, -0.02) * mm, v(29.15, 0.48) * mm, v(30.24, 1.16) * mm, v(31.13, 2.01) * mm]});
            skFitSpline(sketch, "E313", {"points": [v(31.13, 2.01) * mm, v(32.06, 2.9) * mm, v(32.76, 3.9) * mm, v(33.23, 4.98) * mm]});
            skFitSpline(sketch, "E314", {"points": [v(33.23, 4.98) * mm, v(33.73, 6.07) * mm, v(33.98, 7.18) * mm, v(33.98, 8.3) * mm]});
            skFitSpline(sketch, "E315", {"points": [v(33.98, 8.3) * mm, v(33.98, 9.93) * mm, v(33.63, 11.21) * mm, v(32.94, 12.15) * mm]});
            skFitSpline(sketch, "E316", {"points": [v(32.94, 12.15) * mm, v(32.28, 13.08) * mm, v(31.44, 13.8) * mm, v(30.43, 14.3) * mm]});
            skFitSpline(sketch, "E317", {"points": [v(30.43, 14.3) * mm, v(29.42, 14.84) * mm, v(28.32, 15.25) * mm, v(27.11, 15.52) * mm]});
            skFitSpline(sketch, "E318", {"points": [v(27.11, 15.52) * mm, v(25.9, 15.83) * mm, v(24.8, 16.18) * mm, v(23.8, 16.57) * mm]});
            skFitSpline(sketch, "E319", {"points": [v(23.8, 16.57) * mm, v(22.79, 16.96) * mm, v(21.93, 17.48) * mm, v(21.23, 18.14) * mm]});
            skFitSpline(sketch, "E320", {"points": [v(21.23, 18.14) * mm, v(20.57, 18.84) * mm, v(20.24, 19.81) * mm, v(20.24, 21.05) * mm]});
            skFitSpline(sketch, "E321", {"points": [v(20.24, 21.05) * mm, v(20.24, 21.9) * mm, v(20.4, 22.65) * mm, v(20.7, 23.27) * mm]});
            skFitSpline(sketch, "E322", {"points": [v(20.7, 23.27) * mm, v(21.02, 23.89) * mm, v(21.4, 24.4) * mm, v(21.87, 24.78) * mm]});
            skFitSpline(sketch, "E323", {"points": [v(21.87, 24.78) * mm, v(22.34, 25.17) * mm, v(22.86, 25.46) * mm, v(23.44, 25.65) * mm]});
            skFitSpline(sketch, "E324", {"points": [v(23.44, 25.65) * mm, v(24.03, 25.85) * mm, v(24.6, 25.94) * mm, v(25.2, 25.94) * mm]});
            skFitSpline(sketch, "E325", {"points": [v(25.2, 25.94) * mm, v(26.51, 25.94) * mm, v(27.62, 25.58) * mm, v(28.51, 24.84) * mm]});
            skFitSpline(sketch, "E326", {"points": [v(28.51, 24.84) * mm, v(29.4, 24.1) * mm, v(30, 23.27) * mm, v(30.32, 22.33) * mm]});
            skLineSegment(sketch, "E327", {"start": v(17.8, 5.28) * mm, "end": v(17.1, 5.28) * mm});
            skLineSegment(sketch, "E328", {"start": v(17.1, 5.28) * mm, "end": v(17.8, 5.28) * mm});
            skFitSpline(sketch, "E329", {"points": [v(31.01, 22.33) * mm, v(31.1, 22.8) * mm, v(31.27, 23.46) * mm, v(31.54, 24.31) * mm]});
            skFitSpline(sketch, "E330", {"points": [v(31.54, 24.31) * mm, v(31.8, 25.17) * mm, v(32.1, 25.89) * mm, v(32.41, 26.47) * mm]});
            skFitSpline(sketch, "E331", {"points": [v(32.41, 26.47) * mm, v(31.52, 26.78) * mm, v(30.57, 27.13) * mm, v(29.56, 27.52) * mm]});
            skFitSpline(sketch, "E332", {"points": [v(29.56, 27.52) * mm, v(28.59, 27.9) * mm, v(27.38, 28.1) * mm, v(25.95, 28.1) * mm]});
            skFitSpline(sketch, "E333", {"points": [v(25.95, 28.1) * mm, v(24.4, 28.1) * mm, v(23.02, 27.87) * mm, v(21.81, 27.4) * mm]});
            skFitSpline(sketch, "E334", {"points": [v(21.81, 27.4) * mm, v(20.61, 26.97) * mm, v(19.6, 26.37) * mm, v(18.79, 25.6) * mm]});
            skFitSpline(sketch, "E335", {"points": [v(18.79, 25.6) * mm, v(17.97, 24.82) * mm, v(17.35, 23.89) * mm, v(16.92, 22.8) * mm]});
            skFitSpline(sketch, "E336", {"points": [v(16.92, 22.8) * mm, v(16.5, 21.75) * mm, v(16.28, 20.59) * mm, v(16.28, 19.3) * mm]});
            skFitSpline(sketch, "E337", {"points": [v(16.28, 19.3) * mm, v(16.28, 17.68) * mm, v(16.61, 16.4) * mm, v(17.27, 15.46) * mm]});
            skFitSpline(sketch, "E338", {"points": [v(17.27, 15.46) * mm, v(17.97, 14.53) * mm, v(18.83, 13.78) * mm, v(19.84, 13.2) * mm]});
            skFitSpline(sketch, "E339", {"points": [v(19.84, 13.2) * mm, v(20.84, 12.65) * mm, v(21.95, 12.22) * mm, v(23.15, 11.91) * mm]});
            skFitSpline(sketch, "E340", {"points": [v(23.15, 11.91) * mm, v(24.36, 11.6) * mm, v(25.46, 11.23) * mm, v(26.47, 10.8) * mm]});
            skFitSpline(sketch, "E341", {"points": [v(26.47, 10.8) * mm, v(27.48, 10.42) * mm, v(28.32, 9.9) * mm, v(28.98, 9.23) * mm]});
            skFitSpline(sketch, "E342", {"points": [v(28.98, 9.23) * mm, v(29.67, 8.61) * mm, v(30.02, 7.7) * mm, v(30.02, 6.5) * mm]});
            skFitSpline(sketch, "E343", {"points": [v(30.02, 6.5) * mm, v(30.02, 5.64) * mm, v(29.87, 4.89) * mm, v(29.56, 4.23) * mm]});
            skFitSpline(sketch, "E344", {"points": [v(29.56, 4.23) * mm, v(29.25, 3.57) * mm, v(28.82, 3.02) * mm, v(28.28, 2.6) * mm]});
            skFitSpline(sketch, "E345", {"points": [v(28.28, 2.6) * mm, v(27.77, 2.17) * mm, v(27.17, 1.84) * mm, v(26.47, 1.6) * mm]});
            skFitSpline(sketch, "E346", {"points": [v(26.47, 1.6) * mm, v(25.81, 1.37) * mm, v(25.11, 1.26) * mm, v(24.38, 1.26) * mm]});
            skFitSpline(sketch, "E347", {"points": [v(24.38, 1.26) * mm, v(23.56, 1.26) * mm, v(22.79, 1.4) * mm, v(22.05, 1.67) * mm]});
            skFitSpline(sketch, "E348", {"points": [v(22.05, 1.67) * mm, v(21.35, 1.94) * mm, v(20.7, 2.27) * mm, v(20.13, 2.66) * mm]});
            skFitSpline(sketch, "E349", {"points": [v(20.13, 2.66) * mm, v(19.58, 3.08) * mm, v(19.1, 3.53) * mm, v(18.67, 4) * mm]});
            skFitSpline(sketch, "E350", {"points": [v(18.67, 4) * mm, v(18.28, 4.46) * mm, v(18, 4.89) * mm, v(17.8, 5.28) * mm]});
            skLineSegment(sketch, "E351", {"start": v(30.32, 22.33) * mm, "end": v(31.01, 22.33) * mm});
            skLineSegment(sketch, "E352", {"start": v(31.01, 22.33) * mm, "end": v(30.32, 22.33) * mm});
            skFitSpline(sketch, "E353", {"points": [v(37.13, 15.83) * mm, v(37.13, 14.51) * mm, v(37.11, 13.07) * mm, v(37.07, 11.52) * mm]});
            skFitSpline(sketch, "E354", {"points": [v(37.07, 11.52) * mm, v(37.07, 9.97) * mm, v(37.05, 8.44) * mm, v(37.01, 6.92) * mm]});
            skFitSpline(sketch, "E355", {"points": [v(37.01, 6.92) * mm, v(36.97, 5.4) * mm, v(36.92, 3.97) * mm, v(36.84, 2.61) * mm]});
            skFitSpline(sketch, "E356", {"points": [v(36.84, 2.61) * mm, v(36.8, 1.26) * mm, v(36.74, 0.13) * mm, v(36.66, -0.76) * mm]});
            skFitSpline(sketch, "E357", {"points": [v(36.66, -0.76) * mm, v(37.56, -0.69) * mm, v(38.43, -0.65) * mm, v(39.28, -0.65) * mm]});
            skFitSpline(sketch, "E358", {"points": [v(39.28, -0.65) * mm, v(40.14, -0.65) * mm, v(41.01, -0.69) * mm, v(41.9, -0.76) * mm]});
            skFitSpline(sketch, "E359", {"points": [v(41.9, -0.76) * mm, v(41.71, 0.9) * mm, v(41.57, 2.56) * mm, v(41.5, 4.19) * mm]});
            skFitSpline(sketch, "E360", {"points": [v(41.5, 4.19) * mm, v(41.46, 5.85) * mm, v(41.44, 7.56) * mm, v(41.44, 9.3) * mm]});
            skLineSegment(sketch, "E361", {"start": v(37.13, 26.37) * mm, "end": v(37.13, 15.83) * mm});
            skLineSegment(sketch, "E362", {"start": v(37.13, 15.83) * mm, "end": v(37.13, 26.37) * mm});
            skFitSpline(sketch, "E363", {"points": [v(41.44, 12.8) * mm, v(41.44, 13.27) * mm, v(41.63, 13.5) * mm, v(42.02, 13.5) * mm]});
            skFitSpline(sketch, "E364", {"points": [v(42.02, 13.5) * mm, v(42.18, 13.5) * mm, v(42.33, 13.44) * mm, v(42.49, 13.33) * mm]});
            skFitSpline(sketch, "E365", {"points": [v(42.49, 13.33) * mm, v(42.64, 13.21) * mm, v(42.78, 13.07) * mm, v(42.9, 12.92) * mm]});
            skFitSpline(sketch, "E366", {"points": [v(42.9, 12.92) * mm, v(43.6, 12.18) * mm, v(44.43, 11.25) * mm, v(45.4, 10.12) * mm]});
            skFitSpline(sketch, "E367", {"points": [v(45.4, 10.12) * mm, v(46.37, 9) * mm, v(47.38, 7.8) * mm, v(48.43, 6.51) * mm]});
            skFitSpline(sketch, "E368", {"points": [v(48.43, 6.51) * mm, v(49.51, 5.23) * mm, v(50.6, 3.93) * mm, v(51.69, 2.61) * mm]});
            skFitSpline(sketch, "E369", {"points": [v(51.69, 2.61) * mm, v(52.77, 1.33) * mm, v(53.74, 0.2) * mm, v(54.6, -0.76) * mm]});
            skFitSpline(sketch, "E370", {"points": [v(54.6, -0.76) * mm, v(55.14, -0.69) * mm, v(55.66, -0.65) * mm, v(56.17, -0.65) * mm]});
            skFitSpline(sketch, "E371", {"points": [v(56.17, -0.65) * mm, v(56.67, -0.65) * mm, v(57.14, -0.65) * mm, v(57.57, -0.65) * mm]});
            skFitSpline(sketch, "E372", {"points": [v(57.57, -0.65) * mm, v(58.07, -0.65) * mm, v(58.58, -0.65) * mm, v(59.08, -0.65) * mm]});
            skFitSpline(sketch, "E373", {"points": [v(59.08, -0.65) * mm, v(59.62, -0.65) * mm, v(60.23, -0.69) * mm, v(60.89, -0.76) * mm]});
            skFitSpline(sketch, "E374", {"points": [v(60.89, -0.76) * mm, v(58.44, 1.84) * mm, v(56.03, 4.48) * mm, v(53.67, 7.16) * mm]});
            skFitSpline(sketch, "E375", {"points": [v(53.67, 7.16) * mm, v(51.34, 9.83) * mm, v(49.07, 12.51) * mm, v(46.85, 15.2) * mm]});
            skFitSpline(sketch, "E376", {"points": [v(46.85, 15.2) * mm, v(48.87, 17.17) * mm, v(50.99, 19.11) * mm, v(53.2, 21.01) * mm]});
            skFitSpline(sketch, "E377", {"points": [v(53.2, 21.01) * mm, v(55.45, 22.95) * mm, v(57.8, 24.91) * mm, v(60.24, 26.9) * mm]});
            skFitSpline(sketch, "E378", {"points": [v(60.24, 26.9) * mm, v(59.58, 26.82) * mm, v(59.04, 26.74) * mm, v(58.61, 26.66) * mm]});
            skFitSpline(sketch, "E379", {"points": [v(58.61, 26.66) * mm, v(58.19, 26.62) * mm, v(57.76, 26.6) * mm, v(57.33, 26.6) * mm]});
            skFitSpline(sketch, "E380", {"points": [v(57.33, 26.6) * mm, v(56.63, 26.6) * mm, v(55.9, 26.7) * mm, v(55.12, 26.9) * mm]});
            skFitSpline(sketch, "E381", {"points": [v(55.12, 26.9) * mm, v(54.23, 25.85) * mm, v(53.24, 24.74) * mm, v(52.15, 23.57) * mm]});
            skFitSpline(sketch, "E382", {"points": [v(52.15, 23.57) * mm, v(51.06, 22.4) * mm, v(50, 21.3) * mm, v(48.95, 20.26) * mm]});
            skFitSpline(sketch, "E383", {"points": [v(48.95, 20.26) * mm, v(47.94, 19.25) * mm, v(47, 18.35) * mm, v(46.15, 17.58) * mm]});
            skFitSpline(sketch, "E384", {"points": [v(46.15, 17.58) * mm, v(45.34, 16.8) * mm, v(44.76, 16.28) * mm, v(44.4, 16) * mm]});
            skFitSpline(sketch, "E385", {"points": [v(44.4, 16) * mm, v(43.94, 15.66) * mm, v(43.52, 15.35) * mm, v(43.13, 15.07) * mm]});
            skFitSpline(sketch, "E386", {"points": [v(43.13, 15.07) * mm, v(42.78, 14.8) * mm, v(42.45, 14.67) * mm, v(42.14, 14.67) * mm]});
            skFitSpline(sketch, "E387", {"points": [v(42.14, 14.67) * mm, v(41.67, 14.67) * mm, v(41.44, 15.03) * mm, v(41.44, 15.77) * mm]});
            skLineSegment(sketch, "E388", {"start": v(41.44, 9.3) * mm, "end": v(41.44, 12.8) * mm});
            skLineSegment(sketch, "E389", {"start": v(41.44, 12.8) * mm, "end": v(41.44, 9.3) * mm});
            skFitSpline(sketch, "E390", {"points": [v(41.44, 26.37) * mm, v(41.44, 27.69) * mm, v(41.44, 29.13) * mm, v(41.44, 30.68) * mm]});
            skFitSpline(sketch, "E391", {"points": [v(41.44, 30.68) * mm, v(41.48, 32.23) * mm, v(41.52, 33.76) * mm, v(41.55, 35.28) * mm]});
            skFitSpline(sketch, "E392", {"points": [v(41.55, 35.28) * mm, v(41.6, 36.8) * mm, v(41.63, 38.23) * mm, v(41.67, 39.59) * mm]});
            skFitSpline(sketch, "E393", {"points": [v(41.67, 39.59) * mm, v(41.75, 40.98) * mm, v(41.83, 42.17) * mm, v(41.9, 43.14) * mm]});
            skFitSpline(sketch, "E394", {"points": [v(41.9, 43.14) * mm, v(40.82, 42.94) * mm, v(39.94, 42.85) * mm, v(39.28, 42.85) * mm]});
            skFitSpline(sketch, "E395", {"points": [v(39.28, 42.85) * mm, v(38.62, 42.85) * mm, v(37.75, 42.94) * mm, v(36.66, 43.14) * mm]});
            skFitSpline(sketch, "E396", {"points": [v(36.66, 43.14) * mm, v(36.74, 42.17) * mm, v(36.8, 40.98) * mm, v(36.84, 39.59) * mm]});
            skFitSpline(sketch, "E397", {"points": [v(36.84, 39.59) * mm, v(36.92, 38.23) * mm, v(36.97, 36.8) * mm, v(37.01, 35.28) * mm]});
            skFitSpline(sketch, "E398", {"points": [v(37.01, 35.28) * mm, v(37.05, 33.76) * mm, v(37.07, 32.23) * mm, v(37.07, 30.68) * mm]});
            skFitSpline(sketch, "E399", {"points": [v(37.07, 30.68) * mm, v(37.11, 29.13) * mm, v(37.13, 27.69) * mm, v(37.13, 26.37) * mm]});
            skLineSegment(sketch, "E400", {"start": v(41.44, 15.77) * mm, "end": v(41.44, 26.37) * mm});
            skLineSegment(sketch, "E401", {"start": v(41.44, 26.37) * mm, "end": v(41.44, 15.77) * mm});
            skSolve(sketch);
        }
        {
            var Q0;
            Q0=makeQuery(id+"F0.imprint","IMPRINT",FACE,{"disambiguationData":[TD([[makeQuery(id+"F0.imprint","IMPRINT",EDGE,{"derivedFrom":sQuery(id+"F0.wireOp",EDGE,"E0")}),1.0]])]});
            var Q1;
            Q1=makeQuery(id+"F0.imprint","IMPRINT",FACE,{"disambiguationData":[TD([[makeQuery(id+"F0.imprint","IMPRINT",EDGE,{"derivedFrom":sQuery(id+"F0.wireOp",EDGE,"E46")}),1.0]])]});
            var Q2;
            Q2=makeQuery(id+"F0.imprint","IMPRINT",FACE,{"disambiguationData":[TD([[makeQuery(id+"F0.imprint","IMPRINT",EDGE,{"derivedFrom":sQuery(id+"F0.wireOp",EDGE,"E78")}),1.0]])]});
            var Q3;
            Q3=makeQuery(id+"F0.imprint","IMPRINT",FACE,{"disambiguationData":[TD([[makeQuery(id+"F0.imprint","IMPRINT",EDGE,{"derivedFrom":sQuery(id+"F0.wireOp",EDGE,"E124")}),1.0]])]});
            var Q4;
            Q4=makeQuery(id+"F0.imprint","IMPRINT",FACE,{"disambiguationData":[TD([[makeQuery(id+"F0.imprint","IMPRINT",EDGE,{"derivedFrom":sQuery(id+"F0.wireOp",EDGE,"E191")}),1.0]])]});
            var Q5;
            Q5=makeQuery(id+"F0.imprint","IMPRINT",FACE,{"disambiguationData":[TD([[makeQuery(id+"F0.imprint","IMPRINT",EDGE,{"derivedFrom":sQuery(id+"F0.wireOp",EDGE,"E235")}),1.0]])]});
            var Q6;
            Q6=makeQuery(id+"F0.imprint","IMPRINT",FACE,{"disambiguationData":[TD([[makeQuery(id+"F0.imprint","IMPRINT",EDGE,{"derivedFrom":sQuery(id+"F0.wireOp",EDGE,"E291")}),1.0]])]});
            var Q7;
            Q7=makeQuery(id+"F0.imprint","IMPRINT",FACE,{"disambiguationData":[TD([[makeQuery(id+"F0.imprint","IMPRINT",EDGE,{"derivedFrom":sQuery(id+"F0.wireOp",EDGE,"E281")}),1.0]])]});
            var Q8;
            Q8=makeQuery(id+"F0.imprint","IMPRINT",FACE,{"disambiguationData":[TD([[makeQuery(id+"F0.imprint","IMPRINT",EDGE,{"derivedFrom":sQuery(id+"F0.wireOp",EDGE,"E307")}),1.0]])]});
            var Q9;
            Q9=makeQuery(id+"F0.imprint","IMPRINT",FACE,{"disambiguationData":[TD([[makeQuery(id+"F0.imprint","IMPRINT",EDGE,{"derivedFrom":sQuery(id+"F0.wireOp",EDGE,"E353")}),1.0]])]});
            extrude(context, id + "F1", {"entities" : qUnion([Q0, Q1, Q2, Q3, Q4, Q5, Q6, Q7, Q8, Q9]), "depth" : 2 * mm, "offsetDistance" : 25 * mm});
        }
    });
